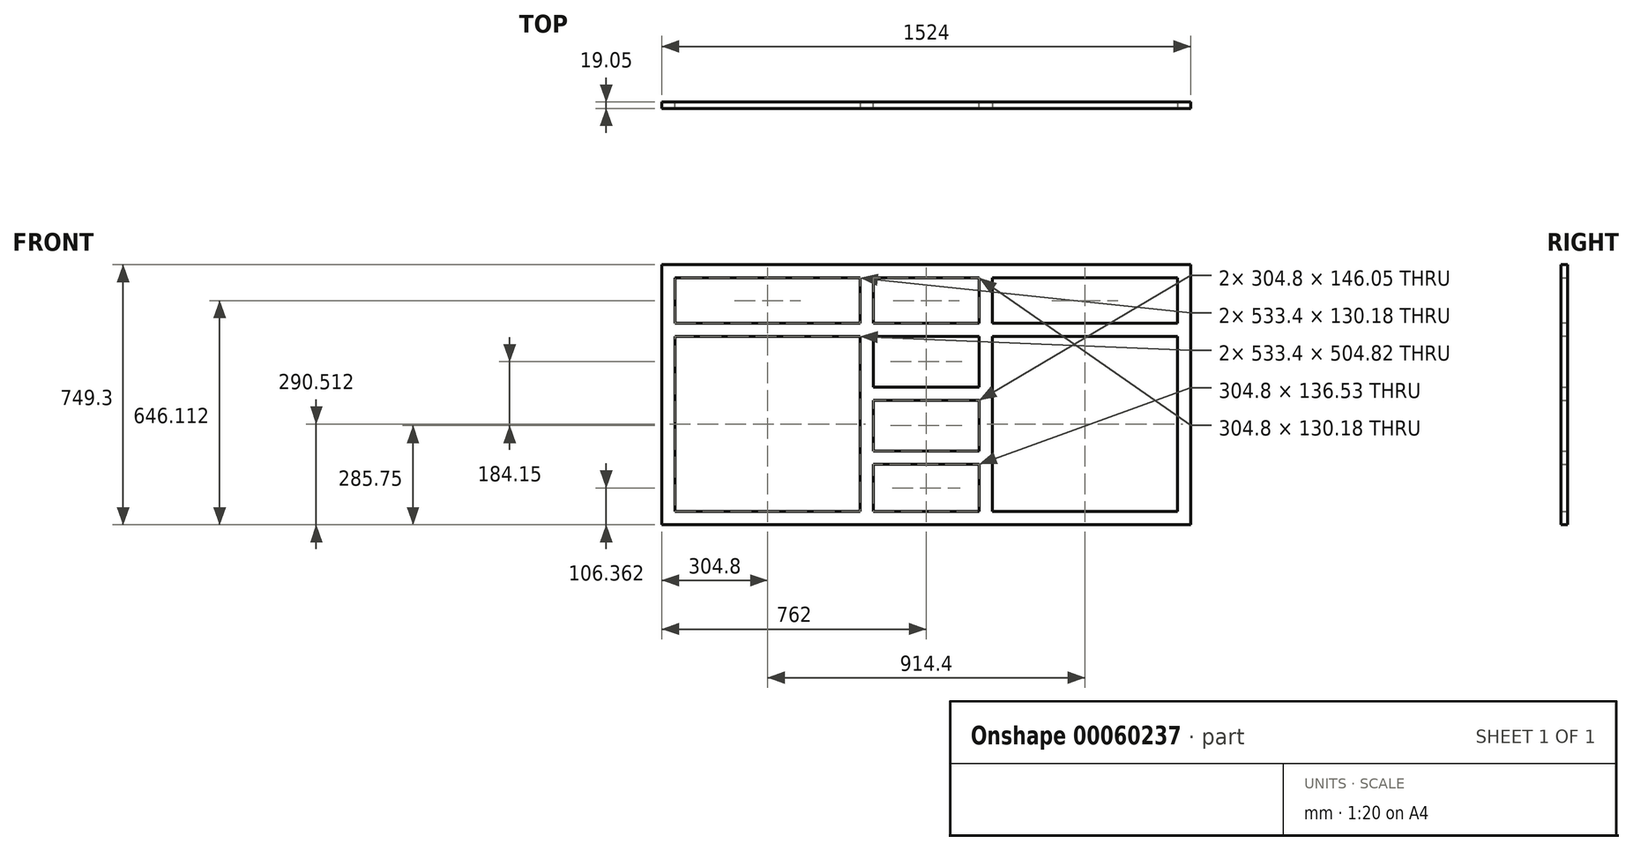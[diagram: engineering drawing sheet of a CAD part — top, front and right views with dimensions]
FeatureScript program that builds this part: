
annotation { "Feature Type Name" : "Feature", "Feature Type Description" : "" }
export const myFeature = defineFeature(function(context is Context, id is Id, definition is map)
    precondition{}
    {
        {
            var Q0;
            Q0=qCreatedBy(makeId("Front.planeOp"),FACE);
            var sketch = newSketch(context, id + "F0", { "sketchPlane" : qUnion([Q0])});
            skLineSegment(sketch, "E0.bottom", {"start": v(0, 0) * mm, "end": v(1524, 0) * mm});
            skLineSegment(sketch, "E0.top", {"start": v(0, 749.3) * mm, "end": v(1524, 749.3) * mm});
            skLineSegment(sketch, "E0.left", {"start": v(0, 0) * mm, "end": v(0, 749.3) * mm});
            skLineSegment(sketch, "E0.right", {"start": v(1524, 0) * mm, "end": v(1524, 749.3) * mm});
            skLineSegment(sketch, "E1.0", {"start": v(38.1, 711.2) * mm, "end": v(571.5, 711.2) * mm});
            skLineSegment(sketch, "E1.1", {"start": v(38.1, 38.1) * mm, "end": v(38.1, 711.2) * mm});
            skLineSegment(sketch, "E1.2", {"start": v(38.1, 38.1) * mm, "end": v(571.5, 38.1) * mm});
            skLineSegment(sketch, "E1.3", {"start": v(1485.9, 38.1) * mm, "end": v(1485.9, 711.2) * mm});
            skLineSegment(sketch, "E2", {"start": v(571.5, 711.2) * mm, "end": v(571.5, 38.1) * mm});
            skLineSegment(sketch, "E3", {"start": v(609.6, 711.2) * mm, "end": v(609.6, 38.1) * mm});
            skLineSegment(sketch, "E4", {"start": v(914.4, 711.2) * mm, "end": v(914.4, 38.1) * mm});
            skLineSegment(sketch, "E5", {"start": v(952.5, 711.2) * mm, "end": v(952.5, 38.1) * mm});
            skLineSegment(sketch, "E6", {"start": v(38.1, 374.65) * mm, "end": v(571.5, 374.65) * mm, "construction": true});
            skLineSegment(sketch, "E7", {"start": v(952.5, 374.65) * mm, "end": v(1485.9, 374.65) * mm, "construction": true});
            skLineSegment(sketch, "E8.trimOffspring", {"start": v(609.6, 38.1) * mm, "end": v(914.4, 38.1) * mm});
            skLineSegment(sketch, "E9.trimOffspring", {"start": v(952.5, 38.1) * mm, "end": v(1485.9, 38.1) * mm});
            skLineSegment(sketch, "E10.trimOffspring", {"start": v(609.6, 711.2) * mm, "end": v(914.4, 711.2) * mm});
            skLineSegment(sketch, "E11.trimOffspring", {"start": v(952.5, 711.2) * mm, "end": v(1485.9, 711.2) * mm});
            skSolve(sketch);
        }
        {
            var Q0;
            Q0=makeQuery(id+"F0.imprint","IMPRINT",FACE,{"disambiguationData":[TD([[makeQuery(id+"F0.imprint","IMPRINT",EDGE,{"derivedFrom":sQuery(id+"F0.wireOp",EDGE,"E0.bottom")}),1.0]])]});
            extrude(context, id + "F1", {"entities" : qUnion([Q0]), "depth" : 19.05 * mm});
        }
        {
            var Q0;
            Q0=makeQuery(id+"F1.opExtrude","SWEPT_FACE",FACE,{"disambiguationData":[OSD([sQuery(id+"F0.wireOp",EDGE,"E1.1")])]});
            var sketch = newSketch(context, id + "F2", { "sketchPlane" : qUnion([Q0])});
            skLineSegment(sketch, "E12.bottom", {"start": v(-19.05, 581.02) * mm, "end": v(0, 581.02) * mm});
            skLineSegment(sketch, "E12.top", {"start": v(-19.05, 542.92) * mm, "end": v(0, 542.92) * mm});
            skLineSegment(sketch, "E12.left", {"start": v(-19.05, 581.02) * mm, "end": v(-19.05, 542.92) * mm});
            skLineSegment(sketch, "E12.right", {"start": v(0, 581.02) * mm, "end": v(0, 542.92) * mm});
            skSolve(sketch);
        }
        {
            var Q0;
            Q0 = qSketchRegion(id + "F2", true);
            var Q1;
            Q1=makeQuery(id+"F1.opExtrude","SWEPT_FACE",FACE,{"disambiguationData":[OSD([sQuery(id+"F0.wireOp",EDGE,"E1.3")])]});
            extrude(context, id + "F3", {"entities" : qUnion([Q0]), "operationType" : NewBodyOperationType.ADD, "endBound" : BoundingType.UP_TO_SURFACE, "endBoundEntityFace" : qUnion([Q1]), "depth" : 25.4 * mm});
        }
        {
            var Q0;
            {var subQ3=sQuery(id+"F0.wireOp",EDGE,"E8.trimOffspring");var subQ6=sQuery(id+"F0.wireOp",EDGE,"E3");Q0=makeQuery(id+"F3.boolean.opBoolean","SPLIT",FACE,{"disambiguationData":[TD([makeQuery(id+"F1.opExtrude","SWEPT_FACE",FACE,{"disambiguationData":[OSD([subQ3])]})])],"derivedFrom":makeQuery(id+"F1.opExtrude","SWEPT_FACE",FACE,{"disambiguationData":[OSD([subQ6])]})});}
            var sketch = newSketch(context, id + "F4", { "sketchPlane" : qUnion([Q0])});
            skLineSegment(sketch, "E13.bottom", {"start": v(-19.05, 396.87) * mm, "end": v(0, 396.87) * mm});
            skLineSegment(sketch, "E13.top", {"start": v(-19.05, 358.77) * mm, "end": v(0, 358.77) * mm});
            skLineSegment(sketch, "E13.left", {"start": v(-19.05, 396.87) * mm, "end": v(-19.05, 358.77) * mm});
            skLineSegment(sketch, "E13.right", {"start": v(0, 396.87) * mm, "end": v(0, 358.77) * mm});
            skSolve(sketch);
        }
        {
            var Q0;
            Q0 = qSketchRegion(id + "F4", true);
            extrude(context, id + "F5", {"entities" : qUnion([Q0]), "operationType" : NewBodyOperationType.ADD, "endBound" : BoundingType.UP_TO_NEXT, "depth" : 25.4 * mm});
        }
        {
            var Q0;
            {var subQ4=sQuery(id+"F0.wireOp",EDGE,"E8.trimOffspring");var subQ7=sQuery(id+"F0.wireOp",EDGE,"E3");var subQ18=makeQuery(id+"F1.opExtrude","SWEPT_FACE",FACE,{"disambiguationData":[OSD([subQ4])]});Q0=makeQuery(id+"F5.boolean.opBoolean","SPLIT",FACE,{"disambiguationData":[TD([subQ18])],"derivedFrom":makeQuery(id+"F3.boolean.opBoolean","SPLIT",FACE,{"disambiguationData":[TD([subQ18])],"derivedFrom":makeQuery(id+"F1.opExtrude","SWEPT_FACE",FACE,{"disambiguationData":[OSD([subQ7])]})})});}
            var sketch = newSketch(context, id + "F6", { "sketchPlane" : qUnion([Q0])});
            skLineSegment(sketch, "E14.bottom", {"start": v(-19.05, 212.72) * mm, "end": v(0, 212.72) * mm});
            skLineSegment(sketch, "E14.top", {"start": v(-19.05, 174.62) * mm, "end": v(0, 174.62) * mm});
            skLineSegment(sketch, "E14.left", {"start": v(-19.05, 212.72) * mm, "end": v(-19.05, 174.62) * mm});
            skLineSegment(sketch, "E14.right", {"start": v(0, 212.72) * mm, "end": v(0, 174.62) * mm});
            skSolve(sketch);
        }
        {
            var Q0;
            Q0 = qSketchRegion(id + "F6", true);
            extrude(context, id + "F7", {"entities" : qUnion([Q0]), "operationType" : NewBodyOperationType.ADD, "endBound" : BoundingType.UP_TO_NEXT, "depth" : 25.4 * mm});
        }
    });
